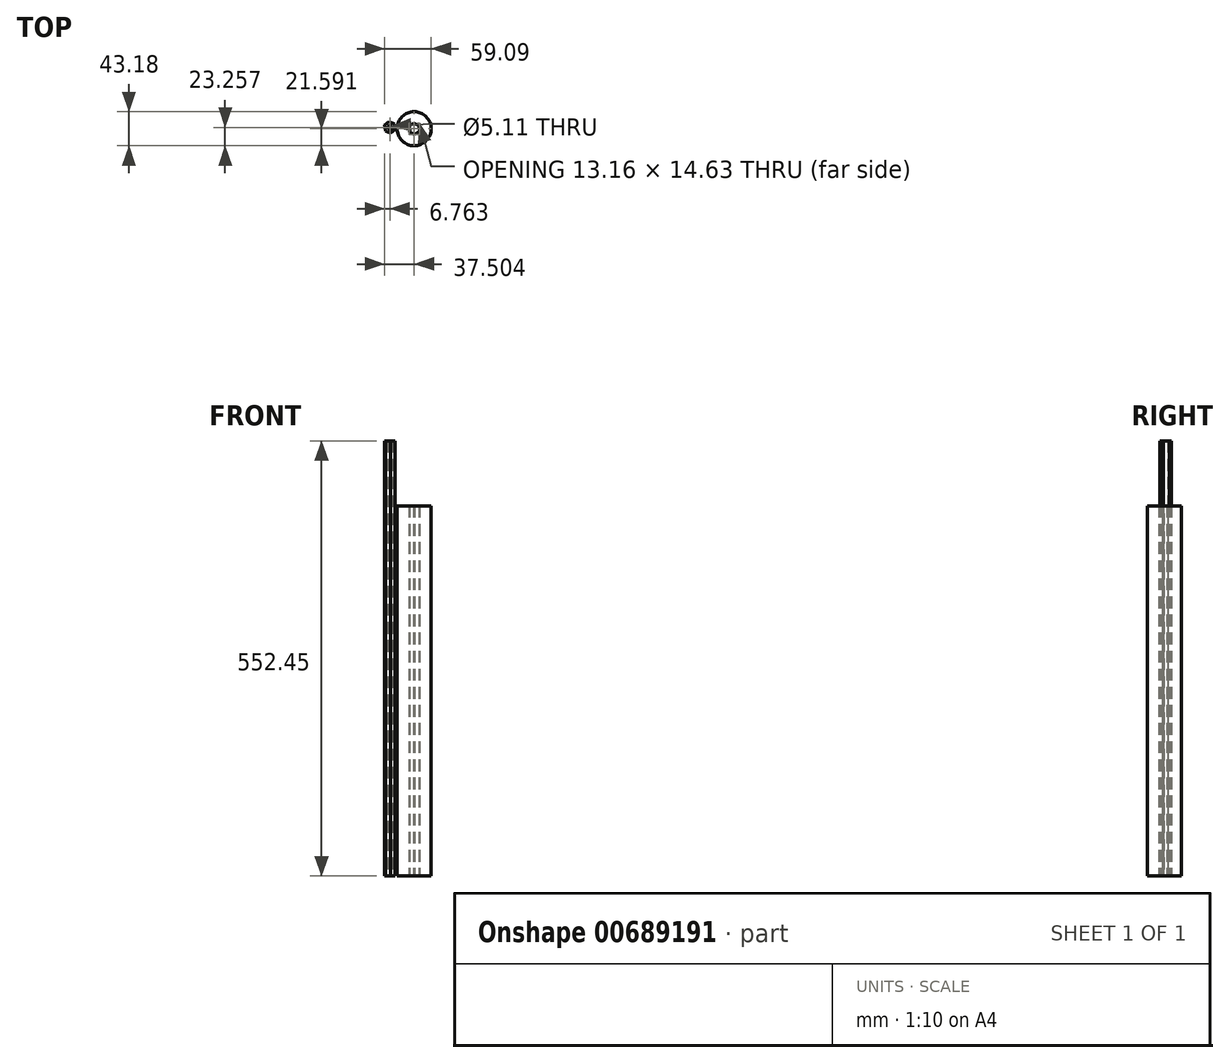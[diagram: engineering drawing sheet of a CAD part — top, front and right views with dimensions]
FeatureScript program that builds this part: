
annotation { "Feature Type Name" : "Feature", "Feature Type Description" : "" }
export const myFeature = defineFeature(function(context is Context, id is Id, definition is map)
    precondition{}
    {
        {
            var Q0;
            Q0=qCreatedBy(makeId("Top.planeOp"),FACE);
            var sketch = newSketch(context, id + "F0", { "sketchPlane" : qUnion([Q0])});
            skCircle(sketch, "E0", {"center": v(-53.7, 57.79) * mm, "radius": 2.55 * mm});
            skCircle(sketch, "E1.cCircle", {"center": v(-53.7, 57.79) * mm, "radius": 6.35 * mm, "construction": true});
            skLineSegment(sketch, "E1.0", {"start": v(-46.94, 54.95) * mm, "end": v(-52.77, 50.51) * mm});
            skLineSegment(sketch, "E1.1", {"start": v(-52.77, 50.51) * mm, "end": v(-59.53, 53.35) * mm});
            skLineSegment(sketch, "E1.2", {"start": v(-59.53, 53.35) * mm, "end": v(-60.46, 60.62) * mm});
            skLineSegment(sketch, "E1.3", {"start": v(-60.46, 60.62) * mm, "end": v(-54.62, 65.06) * mm});
            skLineSegment(sketch, "E1.4", {"start": v(-54.62, 65.06) * mm, "end": v(-47.86, 62.22) * mm});
            skLineSegment(sketch, "E1.5", {"start": v(-47.86, 62.22) * mm, "end": v(-46.94, 54.95) * mm});
            skPoint(sketch, "E1.0.midPoint", {"position": v(-49.85, 52.73) * mm});
            skSolve(sketch);
        }
        {
            var Q0;
            Q0=makeQuery(id+"F0.imprint","IMPRINT",FACE,{"disambiguationData":[TD([[makeQuery(id+"F0.imprint","IMPRINT",EDGE,{"derivedFrom":sQuery(id+"F0.wireOp",EDGE,"E0")}),-1.0]])]});
            extrude(context, id + "F1", {"entities" : qUnion([Q0]), "depth" : 552.45 * mm, "offsetDistance" : 25.4 * mm});
        }
        {
            var Q0;
            Q0=qCreatedBy(makeId("Top.planeOp"),FACE);
            var sketch = newSketch(context, id + "F2", { "sketchPlane" : qUnion([Q0])});
            skCircle(sketch, "E2", {"center": v(-22.96, 56.12) * mm, "radius": 21.59 * mm});
            skCircle(sketch, "E3.cCircle", {"center": v(-22.96, 56.12) * mm, "radius": 6.35 * mm, "construction": true});
            skLineSegment(sketch, "E3.0", {"start": v(-22.47, 48.8) * mm, "end": v(-29.05, 52.04) * mm});
            skLineSegment(sketch, "E3.1", {"start": v(-29.05, 52.04) * mm, "end": v(-29.54, 59.36) * mm});
            skLineSegment(sketch, "E3.2", {"start": v(-29.54, 59.36) * mm, "end": v(-23.44, 63.44) * mm});
            skLineSegment(sketch, "E3.3", {"start": v(-23.44, 63.44) * mm, "end": v(-16.86, 60.2) * mm});
            skLineSegment(sketch, "E3.4", {"start": v(-16.86, 60.2) * mm, "end": v(-16.38, 52.88) * mm});
            skLineSegment(sketch, "E3.5", {"start": v(-16.38, 52.88) * mm, "end": v(-22.47, 48.8) * mm});
            skPoint(sketch, "E3.0.midPoint", {"position": v(-25.76, 50.42) * mm});
            skSolve(sketch);
        }
        {
            var Q0;
            Q0=makeQuery(id+"F2.imprint","IMPRINT",FACE,{"disambiguationData":[TD([[makeQuery(id+"F2.imprint","IMPRINT",EDGE,{"derivedFrom":sQuery(id+"F2.wireOp",EDGE,"E2")}),1.0]])]});
            extrude(context, id + "F3", {"entities" : qUnion([Q0]), "depth" : 469.9 * mm, "offsetDistance" : 25.4 * mm});
        }
    });
